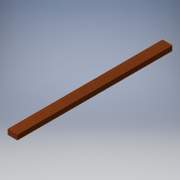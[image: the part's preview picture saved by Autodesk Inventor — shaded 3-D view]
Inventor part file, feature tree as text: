
AUTODESK INVENTOR PART (.ipt)
format: ipt  version: 2016 (Build 200138000, 138)  size: 95,744 bytes
history: native  units: in
note: dims shown in document units (in); Inventor stores cm internally (conversion verified against a paired STEP export)
features: extrude x1, sketch x1
ambient origin geometry x8: Origin, YZ Plane, XZ Plane, XY Plane, X Axis, Y Axis, Z Axis, Center Point
bodies: Solid1 (feature_tree)
feature tree (2):
  extrude  "Extrusion1"  Depth=0.75in
  sketch  "Sketch2"  dims[d0=1.5in d1=0.75in d2=24.0in d3=0.0in]
